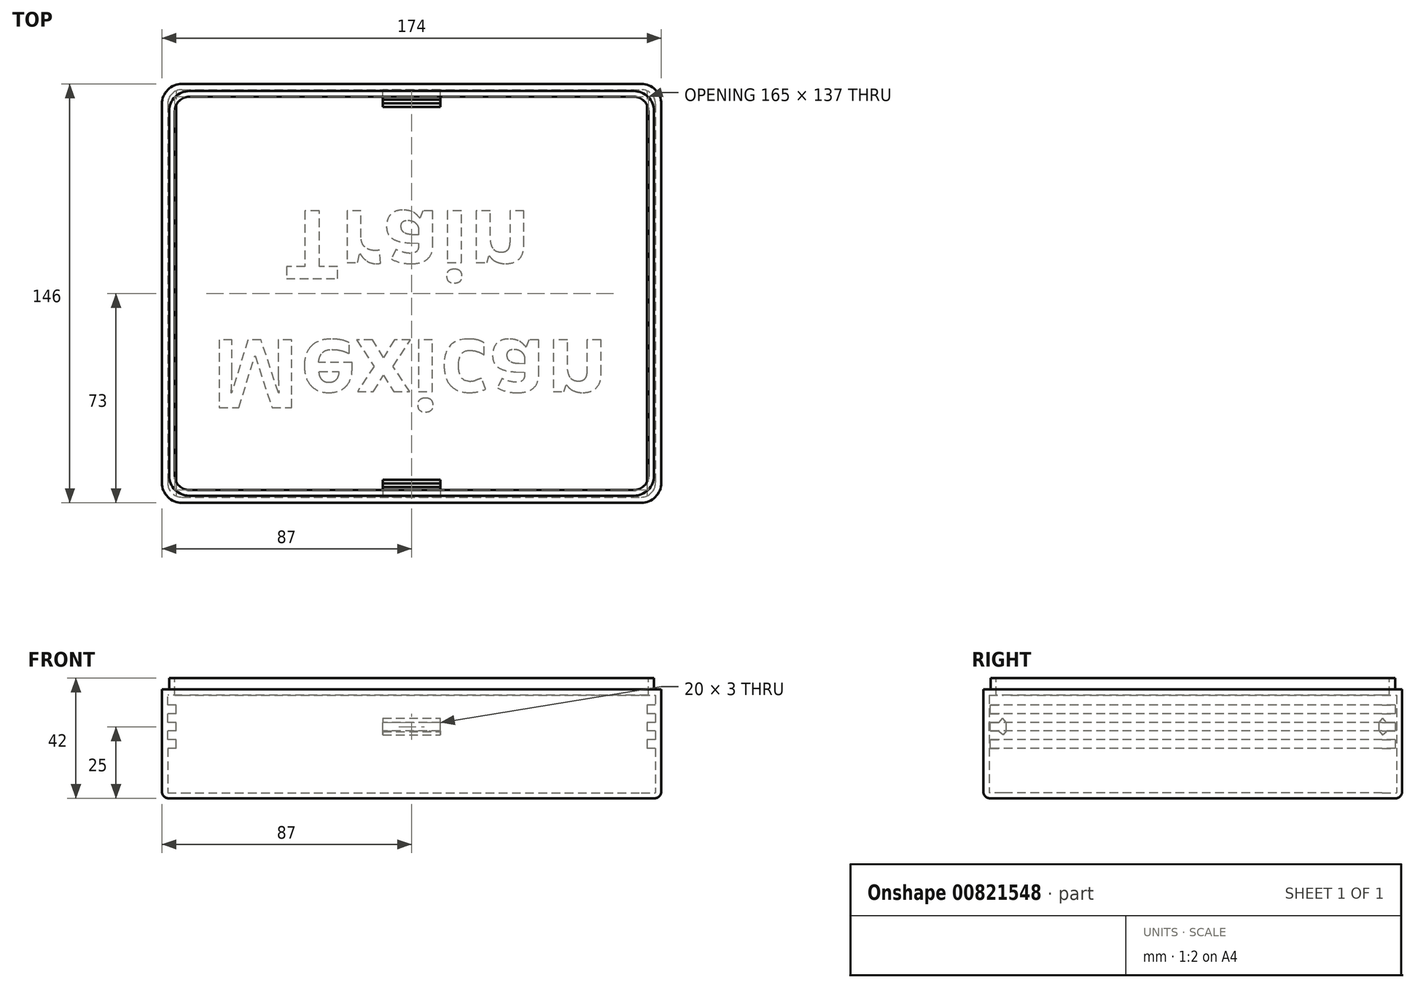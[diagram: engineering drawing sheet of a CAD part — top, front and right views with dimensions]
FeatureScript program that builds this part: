
annotation { "Feature Type Name" : "Feature", "Feature Type Description" : "" }
export const myFeature = defineFeature(function(context is Context, id is Id, definition is map)
    precondition{}
    {
        {
            var Q0;
            Q0=qCreatedBy(makeId("Top.planeOp"),FACE);
            var sketch = newSketch(context, id + "F0", { "sketchPlane" : qUnion([Q0])});
            skLineSegment(sketch, "E0.bottom", {"start": v(87, -73) * mm, "end": v(-87, -73) * mm});
            skLineSegment(sketch, "E0.top", {"start": v(87, 73) * mm, "end": v(-87, 73) * mm});
            skLineSegment(sketch, "E0.left", {"start": v(87, -73) * mm, "end": v(87, 73) * mm});
            skLineSegment(sketch, "E0.right", {"start": v(-87, -73) * mm, "end": v(-87, 73) * mm});
            skPoint(sketch, "E0.middle", {"position": v(0, 0) * mm});
            skLineSegment(sketch, "E1.bottom", {"start": v(85, -71) * mm, "end": v(-85, -71) * mm});
            skLineSegment(sketch, "E1.top", {"start": v(85, 71) * mm, "end": v(-85, 71) * mm});
            skLineSegment(sketch, "E1.left", {"start": v(85, -71) * mm, "end": v(85, 71) * mm});
            skLineSegment(sketch, "E1.right", {"start": v(-85, -71) * mm, "end": v(-85, 71) * mm});
            skSolve(sketch);
        }
        {
            var Q0;
            Q0=qSketchRegion(id+"F0",true);
            var Q1;
            Q1=makeQuery(id+"F0.imprint","IMPRINT",FACE,{"disambiguationData":[TD([[makeQuery(id+"F0.imprint","IMPRINT",EDGE,{"derivedFrom":sQuery(id+"F0.wireOp",EDGE,"E1.bottom")}),-1.0]])]});
            extrude(context, id + "F1", {"entities" : qUnion([Q0, Q1]), "depth" : 2 * mm, "offsetDistance" : 25 * mm});
        }
        {
            var Q0;
            Q0=makeQuery(id+"F0.imprint","IMPRINT",FACE,{"disambiguationData":[TD([[makeQuery(id+"F0.imprint","IMPRINT",EDGE,{"derivedFrom":sQuery(id+"F0.wireOp",EDGE,"E0.bottom")}),-1.0]])]});
            extrude(context, id + "F2", {"entities" : qUnion([Q0]), "operationType" : NewBodyOperationType.ADD, "depth" : 38 * mm, "offsetDistance" : 25 * mm});
        }
        {
            var Q0;
            {var subQ0=sQuery(id+"F0.wireOp",EDGE,"E0.bottom");Q0=makeQuery(id+"F2.boolean.opBoolean","MERGE",FACE,{"derivedFrom":[makeQuery(id+"F1.opExtrude","SWEPT_FACE",FACE,{"disambiguationData":[OSD([subQ0])]}),makeQuery(id+"F2.opExtrude","SWEPT_FACE",FACE,{"disambiguationData":[OSD([subQ0])]})]});}
            var sketch = newSketch(context, id + "F3", { "sketchPlane" : qUnion([Q0])});
            skLineSegment(sketch, "E2.bottom", {"start": v(-87, 38) * mm, "end": v(87, 38) * mm});
            skLineSegment(sketch, "E2.top", {"start": v(-87, 36) * mm, "end": v(87, 36) * mm});
            skLineSegment(sketch, "E2.left", {"start": v(-87, 38) * mm, "end": v(-87, 36) * mm});
            skLineSegment(sketch, "E2.right", {"start": v(87, 38) * mm, "end": v(87, 36) * mm});
            skSolve(sketch);
        }
        {
            var Q0;
            Q0=makeQuery(id+"F3.imprint","IMPRINT",FACE,{"disambiguationData":[TD([[makeQuery(id+"F3.imprint","IMPRINT",EDGE,{"derivedFrom":sQuery(id+"F3.wireOp",EDGE,"E2.bottom")}),1.0]])]});
            extrude(context, id + "F4", {"entities" : qUnion([Q0]), "operationType" : NewBodyOperationType.ADD, "oppositeDirection" : true, "depth" : 146 * mm, "offsetDistance" : 25 * mm});
        }
        {
            var Q0;
            Q0=makeQuery(id+"F4.boolean.opBoolean","MERGE",FACE,{"derivedFrom":[makeQuery(id+"F2.opExtrude","CAP_FACE",FACE,{"disambiguationData":[OSD([sQuery(id+"F0.wireOp",EDGE,"E0.bottom"),sQuery(id+"F0.wireOp",EDGE,"E0.top"),sQuery(id+"F0.wireOp",EDGE,"E0.left"),sQuery(id+"F0.wireOp",EDGE,"E0.right"),sQuery(id+"F0.wireOp",EDGE,"E1.bottom"),sQuery(id+"F0.wireOp",EDGE,"E1.top"),sQuery(id+"F0.wireOp",EDGE,"E1.left"),sQuery(id+"F0.wireOp",EDGE,"E1.right")])],"isStart":false}),makeQuery(id+"F4.opExtrude","SWEPT_FACE",FACE,{"disambiguationData":[OSD([sQuery(id+"F3.wireOp",EDGE,"E2.bottom")])]})]});
            var sketch = newSketch(context, id + "F5", { "sketchPlane" : qUnion([Q0])});
            skLineSegment(sketch, "E3.bottom", {"start": v(82.5, -68.5) * mm, "end": v(-82.5, -68.5) * mm});
            skLineSegment(sketch, "E3.top", {"start": v(82.5, 68.5) * mm, "end": v(-82.5, 68.5) * mm});
            skLineSegment(sketch, "E3.left", {"start": v(82.5, -68.5) * mm, "end": v(82.5, 68.5) * mm});
            skLineSegment(sketch, "E3.right", {"start": v(-82.5, -68.5) * mm, "end": v(-82.5, 68.5) * mm});
            skPoint(sketch, "E3.middle", {"position": v(0, 0) * mm});
            skSolve(sketch);
        }
        {
            var Q0;
            Q0=makeQuery(id+"F5.imprint","IMPRINT",FACE,{"disambiguationData":[TD([[makeQuery(id+"F5.imprint","IMPRINT",EDGE,{"derivedFrom":sQuery(id+"F5.wireOp",EDGE,"E3.bottom")}),-1.0]])]});
            extrude(context, id + "F6", {"entities" : qUnion([Q0]), "operationType" : NewBodyOperationType.REMOVE, "oppositeDirection" : true, "depth" : 2 * mm, "offsetDistance" : 25 * mm});
        }
        {
            var Q0;
            Q0=makeQuery(id+"F4.boolean.opBoolean","MERGE",FACE,{"derivedFrom":[makeQuery(id+"F2.opExtrude","CAP_FACE",FACE,{"disambiguationData":[OSD([sQuery(id+"F0.wireOp",EDGE,"E0.bottom"),sQuery(id+"F0.wireOp",EDGE,"E0.top"),sQuery(id+"F0.wireOp",EDGE,"E0.left"),sQuery(id+"F0.wireOp",EDGE,"E0.right"),sQuery(id+"F0.wireOp",EDGE,"E1.bottom"),sQuery(id+"F0.wireOp",EDGE,"E1.top"),sQuery(id+"F0.wireOp",EDGE,"E1.left"),sQuery(id+"F0.wireOp",EDGE,"E1.right")])],"isStart":false}),makeQuery(id+"F4.opExtrude","SWEPT_FACE",FACE,{"disambiguationData":[OSD([sQuery(id+"F3.wireOp",EDGE,"E2.bottom")])]})]});
            var sketch = newSketch(context, id + "F7", { "sketchPlane" : qUnion([Q0])});
            skLineSegment(sketch, "E4.bottom", {"start": v(84.5, -70.5) * mm, "end": v(-84.5, -70.5) * mm});
            skLineSegment(sketch, "E4.top", {"start": v(84.5, 70.5) * mm, "end": v(-84.5, 70.5) * mm});
            skLineSegment(sketch, "E4.left", {"start": v(84.5, -70.5) * mm, "end": v(84.5, 70.5) * mm});
            skLineSegment(sketch, "E4.right", {"start": v(-84.5, -70.5) * mm, "end": v(-84.5, 70.5) * mm});
            skPoint(sketch, "E4.middle", {"position": v(0, 0) * mm});
            skSolve(sketch);
        }
        {
            var Q0;
            Q0=makeQuery(id+"F7.imprint","IMPRINT",FACE,{"disambiguationData":[TD([[makeQuery(id+"F7.imprint","IMPRINT",EDGE,{"derivedFrom":sQuery(id+"F7.wireOp",EDGE,"E4.bottom")}),-1.0]])]});
            extrude(context, id + "F8", {"entities" : qUnion([Q0]), "operationType" : NewBodyOperationType.ADD, "depth" : 4 * mm, "offsetDistance" : 25 * mm});
        }
        {
            var Q0;
            Q0=makeQuery(id+"F1.opExtrude","CAP_FACE",FACE,{"disambiguationData":[OSD([sQuery(id+"F0.wireOp",EDGE,"E0.bottom"),sQuery(id+"F0.wireOp",EDGE,"E0.top"),sQuery(id+"F0.wireOp",EDGE,"E0.left"),sQuery(id+"F0.wireOp",EDGE,"E0.right")])],"isStart":true});
            fillet(context, id + "F9", {"entities" : qUnion([Q0]), "radius" : 2.5 * mm, "tangentPropagation" : true, "allowEdgeOverflow" : false});
        }
        {
            var Q0;
            Q0=makeQuery(id+"F1.opExtrude","CAP_FACE",FACE,{"disambiguationData":[OSD([sQuery(id+"F0.wireOp",EDGE,"E0.bottom"),sQuery(id+"F0.wireOp",EDGE,"E0.top"),sQuery(id+"F0.wireOp",EDGE,"E0.left"),sQuery(id+"F0.wireOp",EDGE,"E0.right")])],"isStart":true});
            var sketch = newSketch(context, id + "F10", { "sketchPlane" : qUnion([Q0])});
            skText(sketch, "E5", { "text": "Mexican\n   Train", "fontName": "OpenSans-Bold.ttf"});
            skLineSegment(sketch, "E6", {"start": v(0, 0) * mm, "end": v(0, 40) * mm, "construction": true});
            skLineSegment(sketch, "E7", {"start": v(0, 40) * mm, "end": v(-70, 40) * mm, "construction": true});
            const initialGuessF10  = {"E5": [-0.07, 0.01621, 1, 0, 0.02379]};
            skSetInitialGuess(sketch, initialGuessF10);
            skSolve(sketch);
        }
        {
            var Q0;
            Q0=qSketchRegion(id+"F10",true);
            extrude(context, id + "F11", {"entities" : qUnion([Q0]), "operationType" : NewBodyOperationType.REMOVE, "oppositeDirection" : true, "depth" : .1 * mm, "offsetDistance" : 25 * mm});
        }
        {
            var Q0;
            {var subQ0=sQuery(id+"F0.wireOp",EDGE,"E0.bottom");Q0=makeQuery(id+"F2.boolean.opBoolean","MERGE",FACE,{"derivedFrom":[makeQuery(id+"F1.opExtrude","SWEPT_FACE",FACE,{"disambiguationData":[OSD([subQ0])]}),makeQuery(id+"F2.opExtrude","SWEPT_FACE",FACE,{"disambiguationData":[OSD([subQ0])]})]});}
            var sketch = newSketch(context, id + "F12", { "sketchPlane" : qUnion([Q0])});
            skLineSegment(sketch, "E8", {"start": v(-87, 2.5) * mm, "end": v(-87, 17.5) * mm, "construction": true});
            skLineSegment(sketch, "E9.bottom", {"start": v(-87, 17.5) * mm, "end": v(-82, 17.5) * mm});
            skLineSegment(sketch, "E9.top", {"start": v(-87, 20.5) * mm, "end": v(-82, 20.5) * mm});
            skLineSegment(sketch, "E9.left", {"start": v(-87, 17.5) * mm, "end": v(-87, 20.5) * mm});
            skLineSegment(sketch, "E9.right", {"start": v(-82, 17.5) * mm, "end": v(-82, 20.5) * mm});
            skLineSegment(sketch, "E10.top", {"start": v(-87, 23.5) * mm, "end": v(-82, 23.5) * mm});
            skLineSegment(sketch, "E10.left", {"start": v(-87, 20.5) * mm, "end": v(-87, 23.5) * mm});
            skLineSegment(sketch, "E10.right", {"start": v(-82, 20.5) * mm, "end": v(-82, 23.5) * mm});
            skLineSegment(sketch, "E11.top", {"start": v(-87, 26.5) * mm, "end": v(-82, 26.5) * mm});
            skLineSegment(sketch, "E11.left", {"start": v(-87, 23.5) * mm, "end": v(-87, 26.5) * mm});
            skLineSegment(sketch, "E11.right", {"start": v(-82, 23.5) * mm, "end": v(-82, 26.5) * mm});
            skLineSegment(sketch, "E12.top", {"start": v(-87, 29.5) * mm, "end": v(-82, 29.5) * mm});
            skLineSegment(sketch, "E12.left", {"start": v(-87, 26.5) * mm, "end": v(-87, 29.5) * mm});
            skLineSegment(sketch, "E12.right", {"start": v(-82, 26.5) * mm, "end": v(-82, 29.5) * mm});
            skLineSegment(sketch, "E13.top", {"start": v(-87, 32.5) * mm, "end": v(-82, 32.5) * mm});
            skLineSegment(sketch, "E13.left", {"start": v(-87, 29.5) * mm, "end": v(-87, 32.5) * mm});
            skLineSegment(sketch, "E13.right", {"start": v(-82, 29.5) * mm, "end": v(-82, 32.5) * mm});
            skLineSegment(sketch, "E14.bottom", {"start": v(82, 17.5) * mm, "end": v(87, 17.5) * mm});
            skLineSegment(sketch, "E14.top", {"start": v(82, 20.5) * mm, "end": v(87, 20.5) * mm});
            skLineSegment(sketch, "E14.left", {"start": v(82, 17.5) * mm, "end": v(82, 20.5) * mm});
            skLineSegment(sketch, "E14.right", {"start": v(87, 17.5) * mm, "end": v(87, 20.5) * mm});
            skLineSegment(sketch, "E15.top", {"start": v(82, 23.5) * mm, "end": v(87, 23.5) * mm});
            skLineSegment(sketch, "E15.left", {"start": v(82, 20.5) * mm, "end": v(82, 23.5) * mm});
            skLineSegment(sketch, "E15.right", {"start": v(87, 20.5) * mm, "end": v(87, 23.5) * mm});
            skLineSegment(sketch, "E16.top", {"start": v(82, 26.5) * mm, "end": v(87, 26.5) * mm});
            skLineSegment(sketch, "E16.left", {"start": v(82, 23.5) * mm, "end": v(82, 26.5) * mm});
            skLineSegment(sketch, "E16.right", {"start": v(87, 23.5) * mm, "end": v(87, 26.5) * mm});
            skLineSegment(sketch, "E17.top", {"start": v(82, 29.5) * mm, "end": v(87, 29.5) * mm});
            skLineSegment(sketch, "E17.left", {"start": v(82, 26.5) * mm, "end": v(82, 29.5) * mm});
            skLineSegment(sketch, "E17.right", {"start": v(87, 26.5) * mm, "end": v(87, 29.5) * mm});
            skLineSegment(sketch, "E18.top", {"start": v(82, 32.5) * mm, "end": v(87, 32.5) * mm});
            skLineSegment(sketch, "E18.left", {"start": v(82, 29.5) * mm, "end": v(82, 32.5) * mm});
            skLineSegment(sketch, "E18.right", {"start": v(87, 29.5) * mm, "end": v(87, 32.5) * mm});
            skLineSegment(sketch, "E19", {"start": v(-87, 17.5) * mm, "end": v(87, 17.5) * mm, "construction": true});
            skSolve(sketch);
        }
        {
            var Q0;
            Q0=makeQuery(id+"F12.imprint","IMPRINT",FACE,{"disambiguationData":[TD([[makeQuery(id+"F12.imprint","IMPRINT",EDGE,{"derivedFrom":sQuery(id+"F12.wireOp",EDGE,"E9.bottom")}),1.0]])]});
            var Q1;
            Q1=makeQuery(id+"F12.imprint","IMPRINT",FACE,{"disambiguationData":[TD([[makeQuery(id+"F12.imprint","IMPRINT",EDGE,{"derivedFrom":sQuery(id+"F12.wireOp",EDGE,"E10.top")}),1.0]])]});
            var Q2;
            Q2=makeQuery(id+"F12.imprint","IMPRINT",FACE,{"disambiguationData":[TD([[makeQuery(id+"F12.imprint","IMPRINT",EDGE,{"derivedFrom":sQuery(id+"F12.wireOp",EDGE,"E12.top")}),1.0]])]});
            var Q3;
            Q3=makeQuery(id+"F12.imprint","IMPRINT",FACE,{"disambiguationData":[TD([[makeQuery(id+"F12.imprint","IMPRINT",EDGE,{"derivedFrom":sQuery(id+"F12.wireOp",EDGE,"E14.bottom")}),1.0]])]});
            var Q4;
            Q4=makeQuery(id+"F12.imprint","IMPRINT",FACE,{"disambiguationData":[TD([[makeQuery(id+"F12.imprint","IMPRINT",EDGE,{"derivedFrom":sQuery(id+"F12.wireOp",EDGE,"E15.top")}),1.0]])]});
            var Q5;
            Q5=makeQuery(id+"F12.imprint","IMPRINT",FACE,{"disambiguationData":[TD([[makeQuery(id+"F12.imprint","IMPRINT",EDGE,{"derivedFrom":sQuery(id+"F12.wireOp",EDGE,"E17.top")}),1.0]])]});
            extrude(context, id + "F13", {"entities" : qUnion([Q0, Q1, Q2, Q3, Q4, Q5]), "operationType" : NewBodyOperationType.ADD, "oppositeDirection" : true, "depth" : 146 * mm, "offsetDistance" : 25 * mm});
        }
        {
            var Q0;
            {var subQ0=sQuery(id+"F0.wireOp",EDGE,"E1.top");var subQ1=sQuery(id+"F0.wireOp",EDGE,"E1.right");Q0=makeQuery(id+"F13.boolean.opBoolean","SPLIT",EDGE,{"disambiguationData":[TD([makeQuery(id+"F13.opExtrude","SWEPT_FACE",FACE,{"disambiguationData":[OSD([sQuery(id+"F12.wireOp",EDGE,"E9.bottom")])]})])],"derivedFrom":makeQuery(id+"F2.opExtrude","SWEPT_EDGE",EDGE,{"disambiguationData":[OSD([subQ0,subQ1])]})});}
            var Q1;
            {var subQ0=sQuery(id+"F5.wireOp",EDGE,"E3.right");var subQ1=sQuery(id+"F5.wireOp",EDGE,"E3.top");Q1=makeQuery(id+"F8.boolean.opBoolean","MERGE",EDGE,{"derivedFrom":[makeQuery(id+"F6.boolean.opBoolean","COPY",EDGE,{"derivedFrom":makeQuery(id+"F6.opExtrude","SWEPT_EDGE",EDGE,{"disambiguationData":[OSD([subQ1,subQ0])]})}),makeQuery(id+"F8.opExtrude","SWEPT_EDGE",EDGE,{"disambiguationData":[OSD([subQ1,subQ0])]})]});}
            var Q2;
            {var subQ0=sQuery(id+"F5.wireOp",EDGE,"E3.left");var subQ1=sQuery(id+"F5.wireOp",EDGE,"E3.top");Q2=makeQuery(id+"F8.boolean.opBoolean","MERGE",EDGE,{"derivedFrom":[makeQuery(id+"F6.boolean.opBoolean","COPY",EDGE,{"derivedFrom":makeQuery(id+"F6.opExtrude","SWEPT_EDGE",EDGE,{"disambiguationData":[OSD([subQ1,subQ0])]})}),makeQuery(id+"F8.opExtrude","SWEPT_EDGE",EDGE,{"disambiguationData":[OSD([subQ1,subQ0])]})]});}
            var Q3;
            {var subQ0=sQuery(id+"F0.wireOp",EDGE,"E1.top");var subQ1=sQuery(id+"F0.wireOp",EDGE,"E1.left");Q3=makeQuery(id+"F13.boolean.opBoolean","SPLIT",EDGE,{"disambiguationData":[TD([makeQuery(id+"F4.opExtrude","SWEPT_FACE",FACE,{"disambiguationData":[OSD([sQuery(id+"F3.wireOp",EDGE,"E2.top")])]})])],"derivedFrom":makeQuery(id+"F2.opExtrude","SWEPT_EDGE",EDGE,{"disambiguationData":[OSD([subQ0,subQ1])]})});}
            var Q4;
            {var subQ0=sQuery(id+"F0.wireOp",EDGE,"E1.bottom");var subQ1=sQuery(id+"F0.wireOp",EDGE,"E1.left");Q4=makeQuery(id+"F13.boolean.opBoolean","SPLIT",EDGE,{"disambiguationData":[TD([makeQuery(id+"F13.opExtrude","SWEPT_FACE",FACE,{"disambiguationData":[OSD([sQuery(id+"F12.wireOp",EDGE,"E14.bottom")])]})])],"derivedFrom":makeQuery(id+"F2.opExtrude","SWEPT_EDGE",EDGE,{"disambiguationData":[OSD([subQ0,subQ1])]})});}
            var Q5;
            {var subQ0=sQuery(id+"F5.wireOp",EDGE,"E3.left");var subQ1=sQuery(id+"F5.wireOp",EDGE,"E3.bottom");Q5=makeQuery(id+"F8.boolean.opBoolean","MERGE",EDGE,{"derivedFrom":[makeQuery(id+"F6.boolean.opBoolean","COPY",EDGE,{"derivedFrom":makeQuery(id+"F6.opExtrude","SWEPT_EDGE",EDGE,{"disambiguationData":[OSD([subQ1,subQ0])]})}),makeQuery(id+"F8.opExtrude","SWEPT_EDGE",EDGE,{"disambiguationData":[OSD([subQ1,subQ0])]})]});}
            var Q6;
            {var subQ0=sQuery(id+"F0.wireOp",EDGE,"E1.bottom");var subQ1=sQuery(id+"F0.wireOp",EDGE,"E1.right");Q6=makeQuery(id+"F13.boolean.opBoolean","SPLIT",EDGE,{"disambiguationData":[TD([makeQuery(id+"F13.opExtrude","SWEPT_FACE",FACE,{"disambiguationData":[OSD([sQuery(id+"F12.wireOp",EDGE,"E9.bottom")])]})])],"derivedFrom":makeQuery(id+"F2.opExtrude","SWEPT_EDGE",EDGE,{"disambiguationData":[OSD([subQ0,subQ1])]})});}
            var Q7;
            {var subQ0=sQuery(id+"F5.wireOp",EDGE,"E3.right");var subQ1=sQuery(id+"F5.wireOp",EDGE,"E3.bottom");Q7=makeQuery(id+"F8.boolean.opBoolean","MERGE",EDGE,{"derivedFrom":[makeQuery(id+"F6.boolean.opBoolean","COPY",EDGE,{"derivedFrom":makeQuery(id+"F6.opExtrude","SWEPT_EDGE",EDGE,{"disambiguationData":[OSD([subQ1,subQ0])]})}),makeQuery(id+"F8.opExtrude","SWEPT_EDGE",EDGE,{"disambiguationData":[OSD([subQ1,subQ0])]})]});}
            fillet(context, id + "F14", {"entities" : qUnion([Q0, Q1, Q2, Q3, Q4, Q5, Q6, Q7]), "radius" : 5 * mm, "tangentPropagation" : true, "allowEdgeOverflow" : false});
        }
        {
            var Q0;
            {var subQ0=sQuery(id+"F0.wireOp",EDGE,"E0.left");var subQ1=sQuery(id+"F0.wireOp",EDGE,"E0.top");Q0=makeQuery(id+"F2.boolean.opBoolean","MERGE",EDGE,{"derivedFrom":[makeQuery(id+"F1.opExtrude","SWEPT_EDGE",EDGE,{"disambiguationData":[OSD([subQ1,subQ0])]}),makeQuery(id+"F2.opExtrude","SWEPT_EDGE",EDGE,{"disambiguationData":[OSD([subQ1,subQ0])]})]});}
            var Q1;
            {var subQ0=sQuery(id+"F0.wireOp",EDGE,"E0.left");var subQ1=sQuery(id+"F0.wireOp",EDGE,"E0.bottom");Q1=makeQuery(id+"F2.boolean.opBoolean","MERGE",EDGE,{"derivedFrom":[makeQuery(id+"F1.opExtrude","SWEPT_EDGE",EDGE,{"disambiguationData":[OSD([subQ1,subQ0])]}),makeQuery(id+"F2.opExtrude","SWEPT_EDGE",EDGE,{"disambiguationData":[OSD([subQ1,subQ0])]})]});}
            var Q2;
            {var subQ0=sQuery(id+"F0.wireOp",EDGE,"E0.right");var subQ1=sQuery(id+"F0.wireOp",EDGE,"E0.top");Q2=makeQuery(id+"F2.boolean.opBoolean","MERGE",EDGE,{"derivedFrom":[makeQuery(id+"F1.opExtrude","SWEPT_EDGE",EDGE,{"disambiguationData":[OSD([subQ1,subQ0])]}),makeQuery(id+"F2.opExtrude","SWEPT_EDGE",EDGE,{"disambiguationData":[OSD([subQ1,subQ0])]})]});}
            var Q3;
            {var subQ0=sQuery(id+"F0.wireOp",EDGE,"E0.right");var subQ1=sQuery(id+"F0.wireOp",EDGE,"E0.bottom");Q3=makeQuery(id+"F2.boolean.opBoolean","MERGE",EDGE,{"derivedFrom":[makeQuery(id+"F1.opExtrude","SWEPT_EDGE",EDGE,{"disambiguationData":[OSD([subQ1,subQ0])]}),makeQuery(id+"F2.opExtrude","SWEPT_EDGE",EDGE,{"disambiguationData":[OSD([subQ1,subQ0])]})]});}
            var Q4;
            Q4=makeQuery(id+"F8.opExtrude","SWEPT_EDGE",EDGE,{"disambiguationData":[OSD([sQuery(id+"F7.wireOp",EDGE,"E4.bottom"),sQuery(id+"F7.wireOp",EDGE,"E4.right")])]});
            var Q5;
            Q5=makeQuery(id+"F8.opExtrude","SWEPT_EDGE",EDGE,{"disambiguationData":[OSD([sQuery(id+"F7.wireOp",EDGE,"E4.top"),sQuery(id+"F7.wireOp",EDGE,"E4.right")])]});
            var Q6;
            Q6=makeQuery(id+"F8.opExtrude","SWEPT_EDGE",EDGE,{"disambiguationData":[OSD([sQuery(id+"F7.wireOp",EDGE,"E4.top"),sQuery(id+"F7.wireOp",EDGE,"E4.left")])]});
            var Q7;
            Q7=makeQuery(id+"F8.opExtrude","SWEPT_EDGE",EDGE,{"disambiguationData":[OSD([sQuery(id+"F7.wireOp",EDGE,"E4.bottom"),sQuery(id+"F7.wireOp",EDGE,"E4.left")])]});
            fillet(context, id + "F15", {"entities" : qUnion([Q0, Q1, Q2, Q3, Q4, Q5, Q6, Q7]), "radius" : 7 * mm, "tangentPropagation" : true, "allowEdgeOverflow" : false});
        }
        {
            var Q0;
            {var subQ0=sQuery(id+"F0.wireOp",EDGE,"E0.bottom");Q0=makeQuery(id+"F2.boolean.opBoolean","MERGE",FACE,{"derivedFrom":[makeQuery(id+"F1.opExtrude","SWEPT_FACE",FACE,{"disambiguationData":[OSD([subQ0])]}),makeQuery(id+"F2.opExtrude","SWEPT_FACE",FACE,{"disambiguationData":[OSD([subQ0])]})]});}
            var sketch = newSketch(context, id + "F16", { "sketchPlane" : qUnion([Q0])});
            skLineSegment(sketch, "E20.bottom", {"start": v(10, 23.5) * mm, "end": v(-10, 23.5) * mm});
            skLineSegment(sketch, "E20.top", {"start": v(10, 26.5) * mm, "end": v(-10, 26.5) * mm});
            skLineSegment(sketch, "E20.left", {"start": v(10, 23.5) * mm, "end": v(10, 26.5) * mm});
            skLineSegment(sketch, "E20.right", {"start": v(-10, 23.5) * mm, "end": v(-10, 26.5) * mm});
            skPoint(sketch, "E20.middle", {"position": v(0, 25) * mm});
            skLineSegment(sketch, "E21.0.0", {"start": v(84.5, 0) * mm, "end": v(80, 0) * mm});
            skLineSegment(sketch, "E21.0.1", {"start": v(80, 0) * mm, "end": v(-80, 0) * mm});
            skLineSegment(sketch, "E21.0.2", {"start": v(-80, 0) * mm, "end": v(-84.5, 0) * mm});
            skLineSegment(sketch, "E21.0.4", {"start": v(-84.5, 0) * mm, "end": v(-80, 0) * mm});
            skLineSegment(sketch, "E21.0.5", {"start": v(-80, 0) * mm, "end": v(80, 0) * mm});
            skLineSegment(sketch, "E21.0.6", {"start": v(80, 0) * mm, "end": v(84.5, 0) * mm});
            skLineSegment(sketch, "E22", {"start": v(0, 23.5) * mm, "end": v(0, 0) * mm, "construction": true});
            skSolve(sketch);
        }
        {
            var Q0;
            Q0=makeQuery(id+"F16.imprint","IMPRINT",FACE,{"disambiguationData":[TD([[makeQuery(id+"F16.imprint","IMPRINT",EDGE,{"derivedFrom":sQuery(id+"F16.wireOp",EDGE,"E20.bottom")}),-1.0]])]});
            extrude(context, id + "F17", {"entities" : qUnion([Q0]), "oppositeDirection" : true, "depth" : 8 * mm, "offsetDistance" : 25 * mm});
        }
        {
            var Q0;
            Q0=makeQuery(id+"F17.opExtrude","SWEPT_FACE",FACE,{"disambiguationData":[OSD([sQuery(id+"F16.wireOp",EDGE,"E20.top")])]});
            var sketch = newSketch(context, id + "F18", { "sketchPlane" : qUnion([Q0])});
            skLineSegment(sketch, "E23.bottom", {"start": v(10, -65) * mm, "end": v(-10, -65) * mm});
            skLineSegment(sketch, "E23.top", {"start": v(10, -67.5) * mm, "end": v(-10, -67.5) * mm});
            skLineSegment(sketch, "E23.left", {"start": v(10, -65) * mm, "end": v(10, -67.5) * mm});
            skLineSegment(sketch, "E23.right", {"start": v(-10, -65) * mm, "end": v(-10, -67.5) * mm});
            skSolve(sketch);
        }
        {
            var Q0;
            Q0 = qSketchRegion(id + "F18", true);
            extrude(context, id + "F19", {"entities" : qUnion([Q0]), "operationType" : NewBodyOperationType.ADD, "depth" : 1.5 * mm, "offsetDistance" : 25 * mm});
        }
        {
            var Q0;
            Q0=makeQuery(id+"F18.imprint","IMPRINT",FACE,{"disambiguationData":[TD([[makeQuery(id+"F18.imprint","IMPRINT",EDGE,{"derivedFrom":sQuery(id+"F18.wireOp",EDGE,"E23.bottom")}),1.0]])]});
            extrude(context, id + "F20", {"entities" : qUnion([Q0]), "operationType" : NewBodyOperationType.ADD, "oppositeDirection" : true, "depth" : 4.5 * mm, "offsetDistance" : 25 * mm});
        }
        {
            var Q0;
            Q0=makeQuery(id+"F19.opExtrude","CAP_EDGE",EDGE,{"disambiguationData":[OSD([sQuery(id+"F18.wireOp",EDGE,"E23.top")])],"isStart":false});
            var Q1;
            Q1=makeQuery(id+"F19.opExtrude","CAP_EDGE",EDGE,{"disambiguationData":[OSD([sQuery(id+"F18.wireOp",EDGE,"E23.bottom")])],"isStart":false});
            var Q2;
            Q2=makeQuery(id+"F20.opExtrude","CAP_EDGE",EDGE,{"disambiguationData":[OSD([sQuery(id+"F18.wireOp",EDGE,"E23.bottom")])],"isStart":false});
            var Q3;
            Q3=makeQuery(id+"F20.opExtrude","CAP_EDGE",EDGE,{"disambiguationData":[OSD([sQuery(id+"F18.wireOp",EDGE,"E23.top")])],"isStart":false});
            chamfer(context, id + "F21", {"entities" : qUnion([Q0, Q1, Q2, Q3]), "chamferType" : ChamferType.TWO_OFFSETS, "width1" : 1.5 * mm, "oppositeDirection" : false, "width2" : 1.25 * mm, "tangentPropagation" : true});
        }
        {
            var Q0;
            Q0=makeQuery(id+"F19.opExtrude","SWEPT_BODY",BODY,{"disambiguationData":[OSD([sQuery(id+"F18.wireOp",EDGE,"E23.bottom"),sQuery(id+"F18.wireOp",EDGE,"E23.top"),sQuery(id+"F18.wireOp",EDGE,"E23.left"),sQuery(id+"F18.wireOp",EDGE,"E23.right")])]});
            var Q1;
            Q1=makeQuery(id+"F20.opExtrude","SWEPT_BODY",BODY,{"disambiguationData":[OSD([sQuery(id+"F18.wireOp",EDGE,"E23.bottom"),sQuery(id+"F18.wireOp",EDGE,"E23.top"),sQuery(id+"F18.wireOp",EDGE,"E23.left"),sQuery(id+"F18.wireOp",EDGE,"E23.right")])]});
            var Q2;
            Q2=makeQuery(id+"F17.opExtrude","SWEPT_BODY",BODY,{"disambiguationData":[OSD([sQuery(id+"F16.wireOp",EDGE,"E20.bottom"),sQuery(id+"F16.wireOp",EDGE,"E20.top"),sQuery(id+"F16.wireOp",EDGE,"E20.left"),sQuery(id+"F16.wireOp",EDGE,"E20.right")])]});
            var Q3;
            Q3=qCreatedBy(makeId("Front.planeOp"),FACE);
            mirror(context, id + "F22", {"operationType" : NewBodyOperationType.ADD, "entities" : qUnion([Q0, Q1, Q2]), "mirrorPlane" : qUnion([Q3])});
        }
    });
